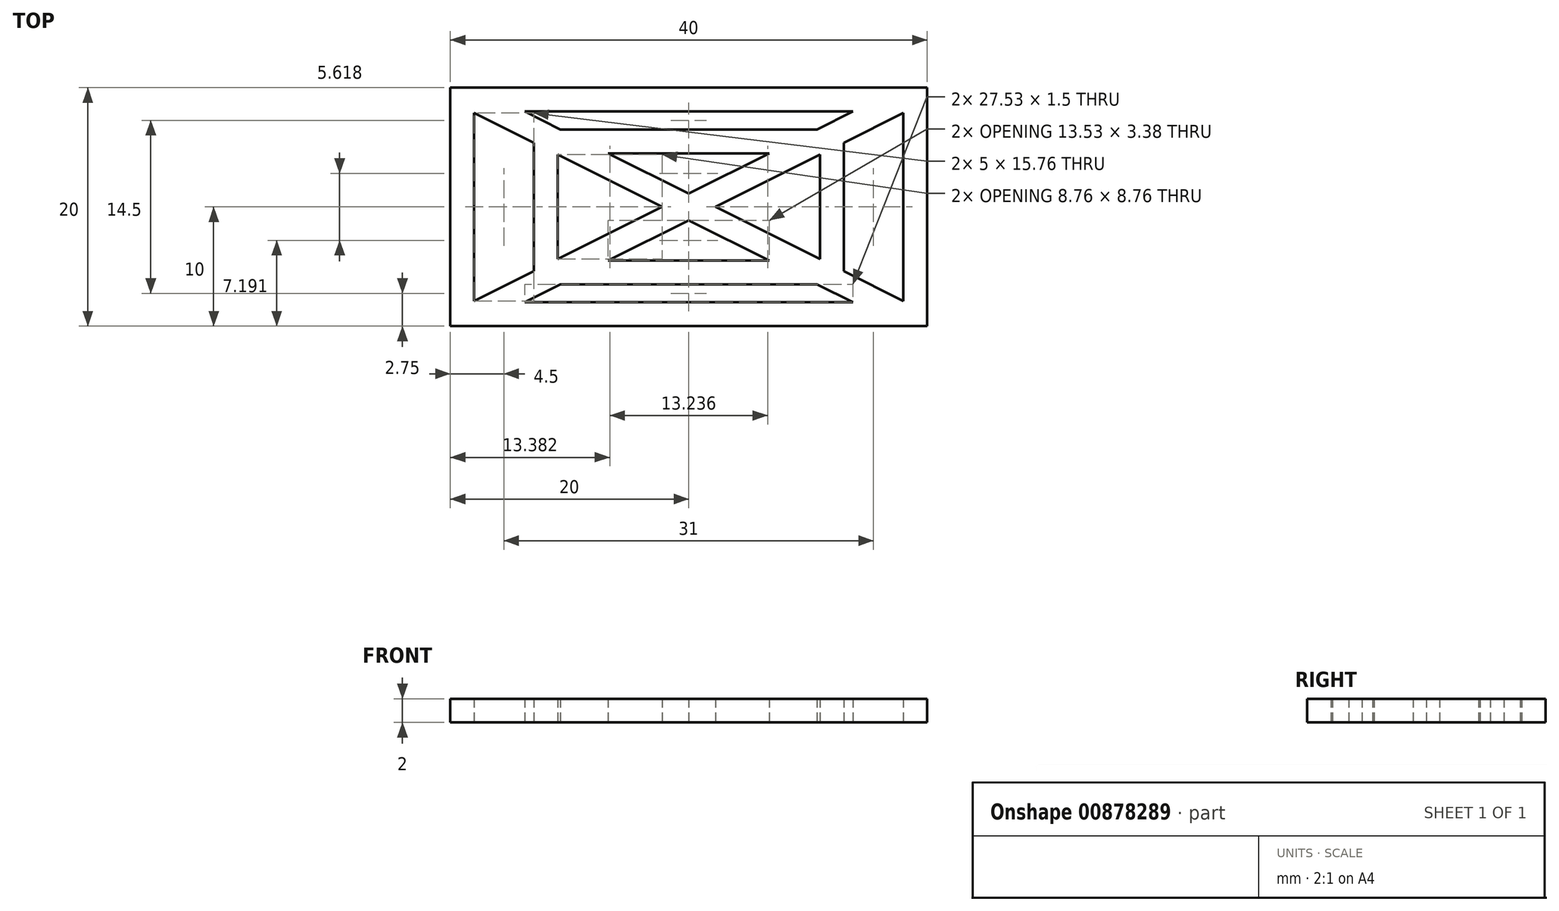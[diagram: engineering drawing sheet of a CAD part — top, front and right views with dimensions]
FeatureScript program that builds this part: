
annotation { "Feature Type Name" : "Feature", "Feature Type Description" : "" }
export const myFeature = defineFeature(function(context is Context, id is Id, definition is map)
    precondition{}
    {
        {
            assignVariable(context, id + "F0", {"name" : "dz_height", "anyValue" : 2 * mm});
        }
        {
            var Q0;
            Q0=qCreatedBy(makeId("Top.planeOp"),FACE);
            var sketch = newSketch(context, id + "F1", { "sketchPlane" : qUnion([Q0])});
            skLineSegment(sketch, "E0.bottom", {"start": v(-20, 10) * mm, "end": v(20, 10) * mm});
            skLineSegment(sketch, "E0.top", {"start": v(-20, -10) * mm, "end": v(20, -10) * mm});
            skLineSegment(sketch, "E0.left", {"start": v(-20, 10) * mm, "end": v(-20, -10) * mm});
            skLineSegment(sketch, "E0.right", {"start": v(20, 10) * mm, "end": v(20, -10) * mm});
            skLineSegment(sketch, "E1", {"start": v(0, 8) * mm, "end": v(0, -8) * mm, "construction": true});
            skLineSegment(sketch, "E2", {"start": v(-20, 10) * mm, "end": v(20, -10) * mm, "construction": true});
            skLineSegment(sketch, "E3", {"start": v(-20, -10) * mm, "end": v(20, 10) * mm, "construction": true});
            skLineSegment(sketch, "E4.bottom", {"start": v(-18, 8) * mm, "end": v(18, 8) * mm});
            skLineSegment(sketch, "E4.top", {"start": v(-18, -8) * mm, "end": v(18, -8) * mm});
            skLineSegment(sketch, "E4.left", {"start": v(-18, 8) * mm, "end": v(-18, -8) * mm});
            skLineSegment(sketch, "E4.right", {"start": v(18, 8) * mm, "end": v(18, -8) * mm});
            skLineSegment(sketch, "E5.bottom", {"start": v(-13, 6.5) * mm, "end": v(13, 6.5) * mm});
            skLineSegment(sketch, "E5.top", {"start": v(-13, -6.5) * mm, "end": v(13, -6.5) * mm});
            skLineSegment(sketch, "E5.left", {"start": v(-13, 6.5) * mm, "end": v(-13, -6.5) * mm});
            skLineSegment(sketch, "E5.right", {"start": v(13, 6.5) * mm, "end": v(13, -6.5) * mm});
            skLineSegment(sketch, "E6.bottom", {"start": v(-11, 4.5) * mm, "end": v(11, 4.5) * mm});
            skLineSegment(sketch, "E6.top", {"start": v(-11, -4.5) * mm, "end": v(11, -4.5) * mm});
            skLineSegment(sketch, "E6.left", {"start": v(-11, 4.5) * mm, "end": v(-11, -4.5) * mm});
            skLineSegment(sketch, "E6.right", {"start": v(11, 4.5) * mm, "end": v(11, -4.5) * mm});
            skLineSegment(sketch, "E7", {"start": v(-17.76, 10) * mm, "end": v(20, -8.88) * mm});
            skLineSegment(sketch, "E8", {"start": v(-20, 8.88) * mm, "end": v(17.76, -10) * mm});
            skLineSegment(sketch, "E9", {"start": v(-20, -8.88) * mm, "end": v(17.76, 10) * mm});
            skLineSegment(sketch, "E10", {"start": v(-17.76, -10) * mm, "end": v(20, 8.88) * mm});
            skLineSegment(sketch, "E11", {"start": v(6.76, 4.5) * mm, "end": v(7.66, 2.71) * mm, "construction": true});
            skPoint(sketch, "E12", {"position": v(7.21, 3.6) * mm});
            skLineSegment(sketch, "E13", {"start": v(7.66, -2.71) * mm, "end": v(6.76, -4.5) * mm, "construction": true});
            skPoint(sketch, "E14", {"position": v(7.21, -3.6) * mm});
            skPoint(sketch, "E15", {"position": v(0, 8) * mm});
            skPoint(sketch, "E16", {"position": v(0, -8) * mm});
            skPoint(sketch, "E17", {"position": v(0, 0) * mm});
            skLineSegment(sketch, "E18", {"start": v(0, 4.5) * mm, "end": v(0, -4.5) * mm, "construction": true});
            skLineSegment(sketch, "E19", {"start": v(-11, 0) * mm, "end": v(11, 0) * mm, "construction": true});
            skSolve(sketch);
        }
        {
            var Q0;
            {var subQ0=sQuery(id+"F1.wireOp",EDGE,"E7");var subQ1=sQuery(id+"F1.wireOp",EDGE,"E0.bottom");var subQ2=makeQuery(id+"F1.imprint","INTERSECT",VERTEX,{"derivedFrom":[subQ1,subQ0]});Q0=makeQuery(id+"F1.imprint","IMPRINT",FACE,{"disambiguationData":[TD([[makeQuery(id+"F1.imprint","IMPRINT",EDGE,{"disambiguationData":[TD([[subQ2,-1.0]])],"derivedFrom":subQ1}),-1.0]])]});}
            var Q1;
            {var subQ0=sQuery(id+"F1.wireOp",EDGE,"E7");var subQ1=sQuery(id+"F1.wireOp",EDGE,"E5.bottom");var subQ2=makeQuery(id+"F1.imprint","INTERSECT",VERTEX,{"derivedFrom":[subQ1,subQ0]});Q1=makeQuery(id+"F1.imprint","IMPRINT",FACE,{"disambiguationData":[TD([[makeQuery(id+"F1.imprint","IMPRINT",EDGE,{"disambiguationData":[TD([[subQ2,-1.0]])],"derivedFrom":subQ1}),-1.0]])]});}
            var Q2;
            {var subQ0=sQuery(id+"F1.wireOp",EDGE,"E8");var subQ1=sQuery(id+"F1.wireOp",EDGE,"E0.left");var subQ2=makeQuery(id+"F1.imprint","INTERSECT",VERTEX,{"derivedFrom":[subQ1,subQ0]});Q2=makeQuery(id+"F1.imprint","IMPRINT",FACE,{"disambiguationData":[TD([[makeQuery(id+"F1.imprint","IMPRINT",EDGE,{"disambiguationData":[TD([[subQ2,-1.0]])],"derivedFrom":subQ1}),1.0]])]});}
            var Q3;
            {var subQ0=sQuery(id+"F1.wireOp",EDGE,"E8");var subQ1=sQuery(id+"F1.wireOp",EDGE,"E5.left");var subQ2=makeQuery(id+"F1.imprint","INTERSECT",VERTEX,{"derivedFrom":[subQ1,subQ0]});Q3=makeQuery(id+"F1.imprint","IMPRINT",FACE,{"disambiguationData":[TD([[makeQuery(id+"F1.imprint","IMPRINT",EDGE,{"disambiguationData":[TD([[subQ2,-1.0]])],"derivedFrom":subQ1}),1.0]])]});}
            var Q4;
            {var subQ5=sQuery(id+"F1.wireOp",EDGE,"E6.left");var subQ6=sQuery(id+"F1.wireOp",EDGE,"E6.top");var subQ7=makeQuery(id+"F1.imprint","INTERSECT",VERTEX,{"derivedFrom":[subQ6,subQ5]});Q4=makeQuery(id+"F1.imprint","IMPRINT",FACE,{"disambiguationData":[TD([[makeQuery(id+"F1.imprint","IMPRINT",EDGE,{"disambiguationData":[TD([[subQ7,-1.0]])],"derivedFrom":subQ6}),1.0]])]});}
            var Q5;
            {var subQ0=sQuery(id+"F1.wireOp",EDGE,"E7");var subQ1=sQuery(id+"F1.wireOp",EDGE,"E0.right");var subQ2=makeQuery(id+"F1.imprint","INTERSECT",VERTEX,{"derivedFrom":[subQ1,subQ0]});Q5=makeQuery(id+"F1.imprint","IMPRINT",FACE,{"disambiguationData":[TD([[makeQuery(id+"F1.imprint","IMPRINT",EDGE,{"disambiguationData":[TD([[subQ2,1.0]])],"derivedFrom":subQ1}),-1.0]])]});}
            var Q6;
            {var subQ1=sQuery(id+"F1.wireOp",EDGE,"E6.right");var subQ6=sQuery(id+"F1.wireOp",EDGE,"E6.top");var subQ9=makeQuery(id+"F1.imprint","INTERSECT",VERTEX,{"derivedFrom":[subQ6,subQ1]});Q6=makeQuery(id+"F1.imprint","IMPRINT",FACE,{"disambiguationData":[TD([[makeQuery(id+"F1.imprint","IMPRINT",EDGE,{"disambiguationData":[TD([[subQ9,1.0]])],"derivedFrom":subQ6}),1.0]])]});}
            var Q7;
            {var subQ1=sQuery(id+"F1.wireOp",EDGE,"E6.bottom");var subQ5=sQuery(id+"F1.wireOp",EDGE,"E6.right");var subQ6=makeQuery(id+"F1.imprint","INTERSECT",VERTEX,{"derivedFrom":[subQ1,subQ5]});Q7=makeQuery(id+"F1.imprint","IMPRINT",FACE,{"disambiguationData":[TD([[makeQuery(id+"F1.imprint","IMPRINT",EDGE,{"disambiguationData":[TD([[subQ6,1.0]])],"derivedFrom":subQ1}),-1.0]])]});}
            var Q8;
            {var subQ7=sQuery(id+"F1.wireOp",EDGE,"E0.left");var subQ8=sQuery(id+"F1.wireOp",EDGE,"E0.bottom");var subQ9=makeQuery(id+"F1.imprint","INTERSECT",VERTEX,{"derivedFrom":[subQ8,subQ7]});Q8=makeQuery(id+"F1.imprint","IMPRINT",FACE,{"disambiguationData":[TD([[makeQuery(id+"F1.imprint","IMPRINT",EDGE,{"disambiguationData":[TD([[subQ9,-1.0]])],"derivedFrom":subQ8}),-1.0]])]});}
            var Q9;
            {var subQ7=sQuery(id+"F1.wireOp",EDGE,"E4.left");var subQ8=sQuery(id+"F1.wireOp",EDGE,"E4.bottom");var subQ9=makeQuery(id+"F1.imprint","INTERSECT",VERTEX,{"derivedFrom":[subQ8,subQ7]});Q9=makeQuery(id+"F1.imprint","IMPRINT",FACE,{"disambiguationData":[TD([[makeQuery(id+"F1.imprint","IMPRINT",EDGE,{"disambiguationData":[TD([[subQ9,-1.0]])],"derivedFrom":subQ8}),-1.0]])]});}
            var Q10;
            {var subQ7=sQuery(id+"F1.wireOp",EDGE,"E5.left");var subQ8=sQuery(id+"F1.wireOp",EDGE,"E5.bottom");var subQ9=makeQuery(id+"F1.imprint","INTERSECT",VERTEX,{"derivedFrom":[subQ8,subQ7]});Q10=makeQuery(id+"F1.imprint","IMPRINT",FACE,{"disambiguationData":[TD([[makeQuery(id+"F1.imprint","IMPRINT",EDGE,{"disambiguationData":[TD([[subQ9,-1.0]])],"derivedFrom":subQ8}),-1.0]])]});}
            var Q11;
            {var subQ7=sQuery(id+"F1.wireOp",EDGE,"E0.right");var subQ8=sQuery(id+"F1.wireOp",EDGE,"E0.bottom");var subQ9=makeQuery(id+"F1.imprint","INTERSECT",VERTEX,{"derivedFrom":[subQ8,subQ7]});Q11=makeQuery(id+"F1.imprint","IMPRINT",FACE,{"disambiguationData":[TD([[makeQuery(id+"F1.imprint","IMPRINT",EDGE,{"disambiguationData":[TD([[subQ9,1.0]])],"derivedFrom":subQ8}),-1.0]])]});}
            var Q12;
            {var subQ7=sQuery(id+"F1.wireOp",EDGE,"E4.right");var subQ8=sQuery(id+"F1.wireOp",EDGE,"E4.bottom");var subQ9=makeQuery(id+"F1.imprint","INTERSECT",VERTEX,{"derivedFrom":[subQ8,subQ7]});Q12=makeQuery(id+"F1.imprint","IMPRINT",FACE,{"disambiguationData":[TD([[makeQuery(id+"F1.imprint","IMPRINT",EDGE,{"disambiguationData":[TD([[subQ9,1.0]])],"derivedFrom":subQ8}),-1.0]])]});}
            var Q13;
            {var subQ7=sQuery(id+"F1.wireOp",EDGE,"E5.right");var subQ8=sQuery(id+"F1.wireOp",EDGE,"E5.bottom");var subQ9=makeQuery(id+"F1.imprint","INTERSECT",VERTEX,{"derivedFrom":[subQ8,subQ7]});Q13=makeQuery(id+"F1.imprint","IMPRINT",FACE,{"disambiguationData":[TD([[makeQuery(id+"F1.imprint","IMPRINT",EDGE,{"disambiguationData":[TD([[subQ9,1.0]])],"derivedFrom":subQ8}),-1.0]])]});}
            var Q14;
            {var subQ0=sQuery(id+"F1.wireOp",EDGE,"E9");var subQ1=sQuery(id+"F1.wireOp",EDGE,"E7");var subQ2=makeQuery(id+"F1.imprint","INTERSECT",VERTEX,{"derivedFrom":[subQ1,subQ0]});Q14=makeQuery(id+"F1.imprint","IMPRINT",FACE,{"disambiguationData":[TD([[makeQuery(id+"F1.imprint","IMPRINT",EDGE,{"disambiguationData":[TD([[subQ2,-1.0]])],"derivedFrom":subQ1}),-1.0]])]});}
            var Q15;
            {var subQ1=sQuery(id+"F1.wireOp",EDGE,"E6.left");var subQ5=sQuery(id+"F1.wireOp",EDGE,"E6.bottom");var subQ6=makeQuery(id+"F1.imprint","INTERSECT",VERTEX,{"derivedFrom":[subQ5,subQ1]});Q15=makeQuery(id+"F1.imprint","IMPRINT",FACE,{"disambiguationData":[TD([[makeQuery(id+"F1.imprint","IMPRINT",EDGE,{"disambiguationData":[TD([[subQ6,-1.0]])],"derivedFrom":subQ5}),-1.0]])]});}
            var Q16;
            {var subQ6=sQuery(id+"F1.wireOp",EDGE,"E5.top");var subQ9=sQuery(id+"F1.wireOp",EDGE,"E5.left");var subQ10=makeQuery(id+"F1.imprint","INTERSECT",VERTEX,{"derivedFrom":[subQ6,subQ9]});Q16=makeQuery(id+"F1.imprint","IMPRINT",FACE,{"disambiguationData":[TD([[makeQuery(id+"F1.imprint","IMPRINT",EDGE,{"disambiguationData":[TD([[subQ10,-1.0]])],"derivedFrom":subQ6}),1.0]])]});}
            var Q17;
            {var subQ6=sQuery(id+"F1.wireOp",EDGE,"E4.top");var subQ9=sQuery(id+"F1.wireOp",EDGE,"E4.left");var subQ10=makeQuery(id+"F1.imprint","INTERSECT",VERTEX,{"derivedFrom":[subQ6,subQ9]});Q17=makeQuery(id+"F1.imprint","IMPRINT",FACE,{"disambiguationData":[TD([[makeQuery(id+"F1.imprint","IMPRINT",EDGE,{"disambiguationData":[TD([[subQ10,-1.0]])],"derivedFrom":subQ6}),1.0]])]});}
            var Q18;
            {var subQ6=sQuery(id+"F1.wireOp",EDGE,"E0.top");var subQ9=sQuery(id+"F1.wireOp",EDGE,"E0.left");var subQ10=makeQuery(id+"F1.imprint","INTERSECT",VERTEX,{"derivedFrom":[subQ6,subQ9]});Q18=makeQuery(id+"F1.imprint","IMPRINT",FACE,{"disambiguationData":[TD([[makeQuery(id+"F1.imprint","IMPRINT",EDGE,{"disambiguationData":[TD([[subQ10,-1.0]])],"derivedFrom":subQ6}),1.0]])]});}
            var Q19;
            {var subQ0=sQuery(id+"F1.wireOp",EDGE,"E8");var subQ1=sQuery(id+"F1.wireOp",EDGE,"E0.top");var subQ2=makeQuery(id+"F1.imprint","INTERSECT",VERTEX,{"derivedFrom":[subQ1,subQ0]});Q19=makeQuery(id+"F1.imprint","IMPRINT",FACE,{"disambiguationData":[TD([[makeQuery(id+"F1.imprint","IMPRINT",EDGE,{"disambiguationData":[TD([[subQ2,1.0]])],"derivedFrom":subQ1}),1.0]])]});}
            var Q20;
            {var subQ5=sQuery(id+"F1.wireOp",EDGE,"E0.right");var subQ9=sQuery(id+"F1.wireOp",EDGE,"E0.top");var subQ10=makeQuery(id+"F1.imprint","INTERSECT",VERTEX,{"derivedFrom":[subQ9,subQ5]});Q20=makeQuery(id+"F1.imprint","IMPRINT",FACE,{"disambiguationData":[TD([[makeQuery(id+"F1.imprint","IMPRINT",EDGE,{"disambiguationData":[TD([[subQ10,1.0]])],"derivedFrom":subQ9}),1.0]])]});}
            var Q21;
            {var subQ7=sQuery(id+"F1.wireOp",EDGE,"E4.right");var subQ8=sQuery(id+"F1.wireOp",EDGE,"E4.top");var subQ9=makeQuery(id+"F1.imprint","INTERSECT",VERTEX,{"derivedFrom":[subQ8,subQ7]});Q21=makeQuery(id+"F1.imprint","IMPRINT",FACE,{"disambiguationData":[TD([[makeQuery(id+"F1.imprint","IMPRINT",EDGE,{"disambiguationData":[TD([[subQ9,1.0]])],"derivedFrom":subQ8}),1.0]])]});}
            var Q22;
            {var subQ7=sQuery(id+"F1.wireOp",EDGE,"E5.top");var subQ9=sQuery(id+"F1.wireOp",EDGE,"E5.right");var subQ10=makeQuery(id+"F1.imprint","INTERSECT",VERTEX,{"derivedFrom":[subQ7,subQ9]});Q22=makeQuery(id+"F1.imprint","IMPRINT",FACE,{"disambiguationData":[TD([[makeQuery(id+"F1.imprint","IMPRINT",EDGE,{"disambiguationData":[TD([[subQ10,1.0]])],"derivedFrom":subQ7}),1.0]])]});}
            var Q23;
            {var subQ0=sQuery(id+"F1.wireOp",EDGE,"E10");var subQ1=sQuery(id+"F1.wireOp",EDGE,"E5.top");var subQ2=makeQuery(id+"F1.imprint","INTERSECT",VERTEX,{"derivedFrom":[subQ1,subQ0]});Q23=makeQuery(id+"F1.imprint","IMPRINT",FACE,{"disambiguationData":[TD([[makeQuery(id+"F1.imprint","IMPRINT",EDGE,{"disambiguationData":[TD([[subQ2,-1.0]])],"derivedFrom":subQ1}),1.0]])]});}
            var Q24;
            {var subQ0=sQuery(id+"F1.wireOp",EDGE,"E10");var subQ1=sQuery(id+"F1.wireOp",EDGE,"E5.right");var subQ2=makeQuery(id+"F1.imprint","INTERSECT",VERTEX,{"derivedFrom":[subQ1,subQ0]});Q24=makeQuery(id+"F1.imprint","IMPRINT",FACE,{"disambiguationData":[TD([[makeQuery(id+"F1.imprint","IMPRINT",EDGE,{"disambiguationData":[TD([[subQ2,-1.0]])],"derivedFrom":subQ1}),-1.0]])]});}
            extrude(context, id + "F2", {"entities" : qUnion([Q0, Q1, Q2, Q3, Q4, Q5, Q6, Q7, Q8, Q9, Q10, Q11, Q12, Q13, Q14, Q15, Q16, Q17, Q18, Q19, Q20, Q21, Q22, Q23, Q24]), "depth" : getVariable(context, 'dz_height'), "offsetDistance" : 25 * mm});
        }
    });
